annotation { "Feature Type Name" : "Feature", "Feature Type Description" : "" }
export const myFeature = defineFeature(function(context is Context, id is Id, definition is map)
    precondition{}
    {
        {
            var Q0;
            Q0=qCreatedBy(makeId("Front.planeOp"),FACE);
            var sketch = newSketch(context, id + "F0", { "sketchPlane" : qUnion([Q0])});
            skLineSegment(sketch, "E0", {"start": v(0, 0) * mm, "end": v(0, 7.94) * mm});
            skLineSegment(sketch, "E1", {"start": v(0, 7.94) * mm, "end": v(29.91, 7.94) * mm});
            skLineSegment(sketch, "E2", {"start": v(36.26, 14.4) * mm, "end": v(35.18, 76.19) * mm});
            skLineSegment(sketch, "E3", {"start": v(38.3, 88.89) * mm, "end": v(38.97, 88.89) * mm});
            skLineSegment(sketch, "E4", {"start": v(41.35, 86.55) * mm, "end": v(42.83, 1.62) * mm});
            skLineSegment(sketch, "E5", {"start": v(41.25, 0) * mm, "end": v(0, 0) * mm});
            skPoint(sketch, "E6.visualSharp", {"position": v(36.37, 7.94) * mm});
            skArc(sketch, "E6.filletArc", {"start": v(29.91, 7.94) * mm, "mid": v(34.44, 9.84) * mm, "end": v(36.26, 14.4) * mm});
            skPoint(sketch, "E7.visualSharp", {"position": v(42.86, 0) * mm});
            skArc(sketch, "E7.filletArc", {"start": v(41.25, 0) * mm, "mid": v(42.38, 0.47) * mm, "end": v(42.83, 1.62) * mm});
            skPoint(sketch, "E8.visualSharp", {"position": v(34.96, 88.89) * mm});
            skPoint(sketch, "E9.visualSharp", {"position": v(41.31, 88.89) * mm});
            skArc(sketch, "E9.filletArc", {"start": v(41.35, 86.55) * mm, "mid": v(40.64, 88.2) * mm, "end": v(38.97, 88.89) * mm});
            skLineSegment(sketch, "E10", {"start": v(35.18, 76.19) * mm, "end": v(35.92, 86.67) * mm});
            skPoint(sketch, "E11.visualSharp", {"position": v(36.07, 88.89) * mm});
            skArc(sketch, "E11.filletArc", {"start": v(38.3, 88.89) * mm, "mid": v(36.67, 88.25) * mm, "end": v(35.92, 86.67) * mm});
            skSolve(sketch);
        }
        {
            var Q0;
            Q0=makeQuery(id+"F0.imprint","IMPRINT",FACE,{"disambiguationData":[TD([[makeQuery(id+"F0.imprint","IMPRINT",EDGE,{"derivedFrom":sQuery(id+"F0.wireOp",EDGE,"E0")}),-1.0]])]});
            var Q1;
            Q1=sQuery(id+"F0.wireOp",EDGE,"E0");
            revolve(context, id + "F1", {"entities" : qUnion([Q0]), "axis" : qUnion([Q1]), "revolveType" : RevolveType.FULL});
        }
        {
            var Q0;
            Q0=qCreatedBy(makeId("Right.planeOp"),FACE);
            cPlane(context, id + "F2", {"entities" : qUnion([Q0]), "cplaneType" : CPlaneType.OFFSET, "offset" : 38.1 * mm, "width" : 152.4 * mm, "height" : 152.4 * mm});
        }
        {
            var Q0;
            Q0=qCreatedBy(id+"F2.planeOp",FACE);
            var sketch = newSketch(context, id + "F3", { "sketchPlane" : qUnion([Q0])});
            skEllipse(sketch, "E12", {"center": v(0, 69.85) * mm, "majorRadius": 10.32 * mm, "minorRadius": 4.76 * mm, "majorAxis": v(1, 0)});
            skSolve(sketch);
        }
        {
            var Q0;
            Q0=qCreatedBy(makeId("Front.planeOp"),FACE);
            var sketch = newSketch(context, id + "F4", { "sketchPlane" : qUnion([Q0])});
            skFitSpline(sketch, "E13", {"points": [v(38.1, 69.85) * mm, v(73.58, 71.5) * mm, v(72.22, 46.63) * mm, v(76.21, 16.26) * mm, v(40.34, 11.54) * mm], "startDerivative": vector(127.15, 70.95) * mm, "endDerivative": vector(-142.7, -7.93) * mm});
            skSolve(sketch);
        }
        {
            var Q0;
            Q0 = qSketchRegion(id + "F3", true);
            var Q1;
            Q1 = qConstructionFilter(qBodyType(qCreatedBy(id + "F4" ,EDGE), BodyType.WIRE), ConstructionObject.NO);
            sweep(context, id + "F5", {"operationType" : NewBodyOperationType.ADD, "profiles" : qUnion([Q0]), "path" : qUnion([Q1])});
        }
        {
            var Q0;
            Q0=makeQuery(id+"F5.boolean.opBoolean","INTERSECT",EDGE,{"disambiguationData":[OD(0.0)],"derivedFrom":[makeQuery(id+"F1.opRevolve","SWEPT_FACE",FACE,{"disambiguationData":[OSD([sQuery(id+"F0.wireOp",EDGE,"E4")])]}),makeQuery(id+"F5.opSweep","SWEPT_FACE",FACE,{"disambiguationData":[OSD([sQuery(id+"F3.wireOp",EDGE,"E12"),sQuery(id+"F4.wireOp",EDGE,"E13")])]})]});
            var Q1;
            Q1=makeQuery(id+"F5.boolean.opBoolean","INTERSECT",EDGE,{"disambiguationData":[OD(1.0)],"derivedFrom":[makeQuery(id+"F1.opRevolve","SWEPT_FACE",FACE,{"disambiguationData":[OSD([sQuery(id+"F0.wireOp",EDGE,"E4")])]}),makeQuery(id+"F5.opSweep","SWEPT_FACE",FACE,{"disambiguationData":[OSD([sQuery(id+"F3.wireOp",EDGE,"E12"),sQuery(id+"F4.wireOp",EDGE,"E13")])]})]});
            fillet(context, id + "F6", {"entities" : qUnion([Q0, Q1]), "radius" : 3.97 * mm, "tangentPropagation" : true, "allowEdgeOverflow" : false});
        }
        {
            var Q0;
            Q0=makeQuery(id+"F1.opRevolve","SWEPT_FACE",FACE,{"disambiguationData":[OSD([sQuery(id+"F0.wireOp",EDGE,"E5")])]});
            var sketch = newSketch(context, id + "F7", { "sketchPlane" : qUnion([Q0])});
            skText(sketch, "E14", { "text": "Digitally Designed\n                &\n        Crafted by\n              PSR", "fontName": "AllertaStencil-Regular.ttf"});
            const initialGuessF7  = {"E14": [-0.0254, 0.00635, 1, 0, 0.0039]};
            skSetInitialGuess(sketch, initialGuessF7);
            skSolve(sketch);
        }
        {
            var Q0;
            Q0 = qSketchRegion(id + "F7", true);
            extrude(context, id + "F8", {"entities" : qUnion([Q0]), "operationType" : NewBodyOperationType.REMOVE, "oppositeDirection" : true, "depth" : 1.59 * mm, "hasDraft" : true, "draftAngle" : 1 * degree, "draftPullDirection" : true});
        }
    });